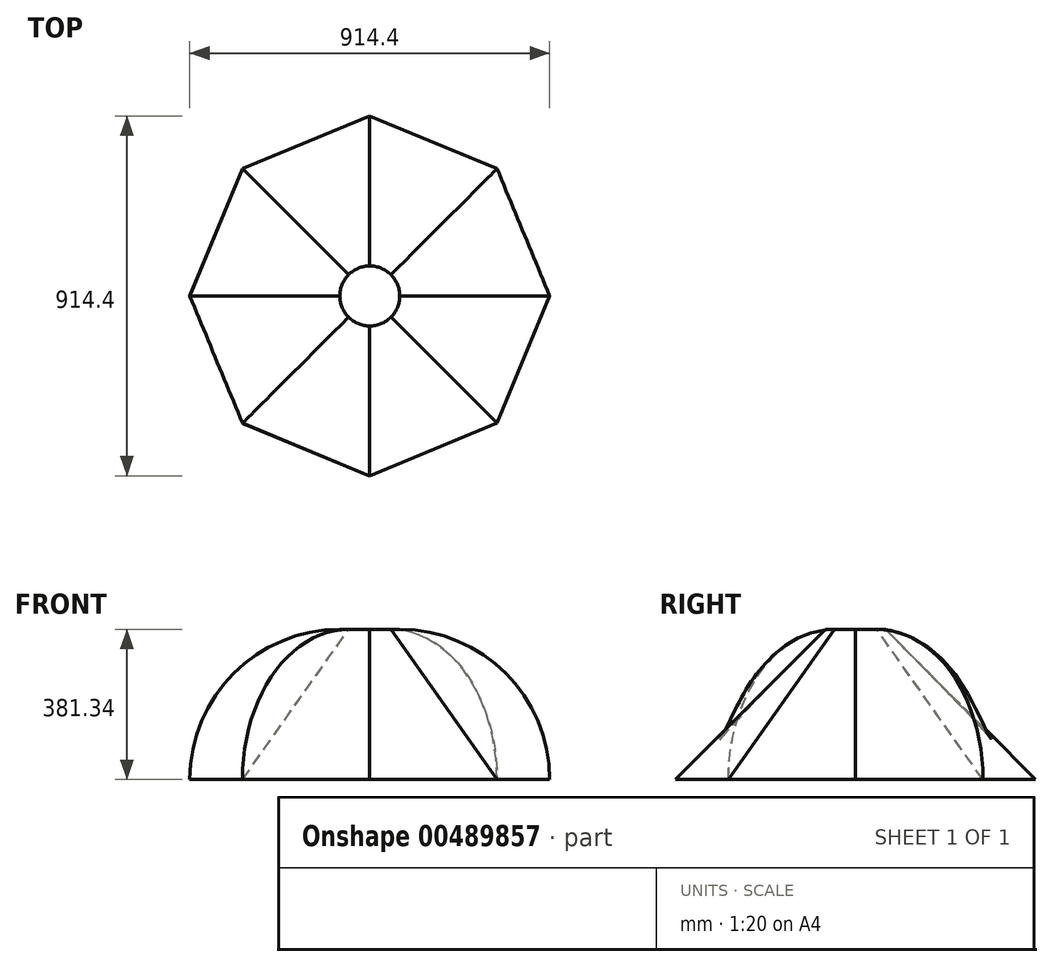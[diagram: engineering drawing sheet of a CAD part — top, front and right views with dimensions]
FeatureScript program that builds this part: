
annotation { "Feature Type Name" : "Feature", "Feature Type Description" : "" }
export const myFeature = defineFeature(function(context is Context, id is Id, definition is map)
    precondition{}
    {
        {
            var Q0;
            Q0=qCreatedBy(makeId("Top.planeOp"),FACE);
            cPlane(context, id + "F0", {"entities" : qUnion([Q0]), "cplaneType" : CPlaneType.OFFSET, "offset" : 381 * mm, "width" : 152.4 * mm, "height" : 152.4 * mm});
        }
        {
            var Q0;
            Q0=qCreatedBy(id+"F0.planeOp",FACE);
            var sketch = newSketch(context, id + "F1", { "sketchPlane" : qUnion([Q0])});
            skCircle(sketch, "E0", {"center": v(0, 0) * mm, "radius": 76.2 * mm});
            skLineSegment(sketch, "E1", {"start": v(0, 76.2) * mm, "end": v(0, -76.2) * mm, "construction": true});
            skLineSegment(sketch, "E2.1.0", {"start": v(53.88, 53.88) * mm, "end": v(-53.88, -53.88) * mm, "construction": true});
            skLineSegment(sketch, "E2.2.0", {"start": v(76.2, 0) * mm, "end": v(-76.2, 0) * mm, "construction": true});
            skLineSegment(sketch, "E2.3.0", {"start": v(53.88, -53.88) * mm, "end": v(-53.88, 53.88) * mm, "construction": true});
            skLineSegment(sketch, "E2.anchor1", {"start": v(0, 0) * mm, "end": v(0, -76.2) * mm, "construction": true});
            skLineSegment(sketch, "E2.anchor2", {"start": v(0, 0) * mm, "end": v(-53.88, 53.88) * mm, "construction": true});
            skSolve(sketch);
        }
        {
            var Q0;
            Q0=qCreatedBy(makeId("Front.planeOp"),FACE);
            var sketch = newSketch(context, id + "F2", { "sketchPlane" : qUnion([Q0])});
            skLineSegment(sketch, "E3", {"start": v(0, 0) * mm, "end": v(0, 381) * mm, "construction": true});
            skSolve(sketch);
        }
        {
            var Q0;
            Q0=qCreatedBy(makeId("Top.planeOp"),FACE);
            var sketch = newSketch(context, id + "F3", { "sketchPlane" : qUnion([Q0])});
            skCircle(sketch, "E4.cCircle", {"center": v(0, 0) * mm, "radius": 422.4 * mm, "construction": true});
            skLineSegment(sketch, "E4.0", {"start": v(323.29, 323.29) * mm, "end": v(457.2, 0) * mm});
            skLineSegment(sketch, "E4.1", {"start": v(457.2, 0) * mm, "end": v(323.29, -323.29) * mm});
            skLineSegment(sketch, "E4.2", {"start": v(323.29, -323.29) * mm, "end": v(0, -457.2) * mm});
            skLineSegment(sketch, "E4.3", {"start": v(0, -457.2) * mm, "end": v(-323.29, -323.29) * mm});
            skLineSegment(sketch, "E4.4", {"start": v(-323.29, -323.29) * mm, "end": v(-457.2, 0) * mm});
            skLineSegment(sketch, "E4.5", {"start": v(-457.2, 0) * mm, "end": v(-323.29, 323.29) * mm});
            skLineSegment(sketch, "E4.6", {"start": v(-323.29, 323.29) * mm, "end": v(0, 457.2) * mm});
            skLineSegment(sketch, "E4.7", {"start": v(0, 457.2) * mm, "end": v(323.29, 323.29) * mm});
            skPoint(sketch, "E4.0.midPoint", {"position": v(390.24, 161.64) * mm});
            skLineSegment(sketch, "E5", {"start": v(0, 457.2) * mm, "end": v(0, -457.2) * mm, "construction": true});
            skSolve(sketch);
        }
        {
            var Q0;
            Q0=qCreatedBy(makeId("Front.planeOp"),FACE);
            var sketch = newSketch(context, id + "F4", { "sketchPlane" : qUnion([Q0])});
            skArc(sketch, "E6", {"start": v(457.2, 0) * mm, "mid": v(345.6, 269.4) * mm, "end": v(76.2, 381) * mm});
            skArc(sketch, "E7.MirrorCS", {"start": v(-457.2, 0) * mm, "mid": v(-345.6, 269.4) * mm, "end": v(-76.2, 381) * mm});
            skSolve(sketch);
        }
        {
            var Q0;
            Q0=qCreatedBy(makeId("Front.planeOp"),FACE);
            var Q1;
            Q1=sQuery(id+"F2.wireOp",EDGE,"E3");
            cPlane(context, id + "F5", {"entities" : qUnion([Q0, Q1]), "cplaneType" : CPlaneType.LINE_ANGLE, "offset" : 25.4 * mm, "angle" : 45 * degree, "width" : 152.4 * mm, "height" : 152.4 * mm});
        }
        {
            var Q0;
            Q0=qCreatedBy(id+"F5.planeOp",FACE);
            var sketch = newSketch(context, id + "F6", { "sketchPlane" : qUnion([Q0])});
            skArc(sketch, "E8", {"start": v(-76.2, 381) * mm, "mid": v(-345.6, 269.4) * mm, "end": v(-457.2, 0) * mm});
            skArc(sketch, "E9.MirrorCS", {"start": v(76.2, 381) * mm, "mid": v(345.6, 269.4) * mm, "end": v(457.2, 0) * mm});
            skSolve(sketch);
        }
        {
            var Q0;
            Q0=qCreatedBy(makeId("Front.planeOp"),FACE);
            var sketch = newSketch(context, id + "F7", { "sketchPlane" : qUnion([Q0])});
            skLineSegment(sketch, "E10", {"start": v(0, 381) * mm, "end": v(0, -533.4) * mm});
            skArc(sketch, "E11", {"start": v(-101.6, -533.4) * mm, "mid": v(-50.8, -584.2) * mm, "end": v(0, -533.4) * mm});
            skSolve(sketch);
        }
        {
            var Q0;
            Q0=qCreatedBy(id+"F0.planeOp",FACE);
            var sketch = newSketch(context, id + "F8", { "sketchPlane" : qUnion([Q0])});
            skCircle(sketch, "E12", {"center": v(0, 0) * mm, "radius": 19.05 * mm});
            skSolve(sketch);
        }
        {
            var Q0;
            Q0=makeQuery(id+"F3.imprint","IMPRINT",FACE,{"disambiguationData":[TD([[makeQuery(id+"F3.imprint","IMPRINT",EDGE,{"derivedFrom":sQuery(id+"F3.wireOp",EDGE,"E4.0")}),-1.0]])]});
            var Q1;
            Q1=makeQuery(id+"F1.imprint","IMPRINT",FACE,{"disambiguationData":[TD([[makeQuery(id+"F1.imprint","IMPRINT",EDGE,{"derivedFrom":sQuery(id+"F1.wireOp",EDGE,"E0")}),1.0]])]});
            var Q2;
            Q2=sQuery(id+"F4.wireOp",EDGE,"E6");
            var Q3;
            Q3=sQuery(id+"FwEUsNg9eqqxYRy_0.1.F6.wireOp",EDGE,"E9.MirrorCS");
            var Q4;
            Q4=sQuery(id+"FwEUsNg9eqqxYRy_0.1.F4.wireOp",EDGE,"E7.MirrorCS");
            var Q5;
            Q5=sQuery(id+"F6.wireOp",EDGE,"E9.MirrorCS");
            var Q6;
            Q6=sQuery(id+"F6.wireOp",EDGE,"E8");
            var Q7;
            Q7=sQuery(id+"FwEUsNg9eqqxYRy_0.1.F4.wireOp",EDGE,"E6");
            var Q8;
            Q8=sQuery(id+"FwEUsNg9eqqxYRy_0.1.F6.wireOp",EDGE,"E8");
            var Q9;
            Q9=sQuery(id+"F4.wireOp",EDGE,"E7.MirrorCS");
            loft(context, id + "F9", {"addGuides" : true, "sheetProfilesArray" : [{ "sheetProfileEntities" : qUnion([Q0]) }, { "sheetProfileEntities" : qUnion([Q1]) }], "guidesArray" : [{ "guideEntities" : qUnion([Q2]), "guideDerivativeType" : LoftGuideDerivativeType.DEFAULT, "guideDerivativeMagnitude" : 1 }, { "guideEntities" : qUnion([Q3]), "guideDerivativeType" : LoftGuideDerivativeType.DEFAULT, "guideDerivativeMagnitude" : 1 }, { "guideEntities" : qUnion([Q4]), "guideDerivativeType" : LoftGuideDerivativeType.DEFAULT, "guideDerivativeMagnitude" : 1 }, { "guideEntities" : qUnion([Q5]), "guideDerivativeType" : LoftGuideDerivativeType.DEFAULT, "guideDerivativeMagnitude" : 1 }, { "guideEntities" : qUnion([Q6]), "guideDerivativeType" : LoftGuideDerivativeType.DEFAULT, "guideDerivativeMagnitude" : 1 }, { "guideEntities" : qUnion([Q7]), "guideDerivativeType" : LoftGuideDerivativeType.DEFAULT, "guideDerivativeMagnitude" : 1 }, { "guideEntities" : qUnion([Q8]), "guideDerivativeType" : LoftGuideDerivativeType.DEFAULT, "guideDerivativeMagnitude" : 1 }, { "guideEntities" : qUnion([Q9]), "guideDerivativeType" : LoftGuideDerivativeType.DEFAULT, "guideDerivativeMagnitude" : 1 }]});
        }
        {
            var Q0;
            Q0=makeQuery(id+"F9.opLoft","CAP_FACE",FACE,{"disambiguationData":[OSD([makeQuery(id+"F3.imprint","IMPRINT",FACE,{"disambiguationData":[TD([[makeQuery(id+"F3.imprint","IMPRINT",EDGE,{"derivedFrom":sQuery(id+"F3.wireOp",EDGE,"E4.0")}),-1.0]])]})])],"isStart":true});
            shell(context, id + "F10", {"entities" : qUnion([Q0]), "thickness" : 0.5 * mm});
        }
        {
            var Q0;
            Q0=makeQuery(id+"F1.imprint","IMPRINT",FACE,{"disambiguationData":[TD([[makeQuery(id+"F1.imprint","IMPRINT",EDGE,{"derivedFrom":sQuery(id+"F1.wireOp",EDGE,"E0")}),1.0]])]});
            var Q1;
            Q1=makeQuery(id+"F3.imprint","IMPRINT",FACE,{"disambiguationData":[TD([[makeQuery(id+"F3.imprint","IMPRINT",EDGE,{"derivedFrom":sQuery(id+"F3.wireOp",EDGE,"E4.0")}),-1.0]])]});
            var Q2;
            Q2=sQuery(id+"F4.wireOp",EDGE,"E6");
            var Q3;
            Q3=sQuery(id+"F4.wireOp",EDGE,"E7.MirrorCS");
            var Q4;
            Q4=sQuery(id+"FwEUsNg9eqqxYRy_0.1.F6.wireOp",EDGE,"E8");
            var Q5;
            Q5=sQuery(id+"FwEUsNg9eqqxYRy_0.1.F4.wireOp",EDGE,"E6");
            var Q6;
            Q6=sQuery(id+"F6.wireOp",EDGE,"E8");
            var Q7;
            Q7=sQuery(id+"FwEUsNg9eqqxYRy_0.1.F6.wireOp",EDGE,"E9.MirrorCS");
            var Q8;
            Q8=sQuery(id+"FwEUsNg9eqqxYRy_0.1.F4.wireOp",EDGE,"E7.MirrorCS");
            var Q9;
            Q9=sQuery(id+"F6.wireOp",EDGE,"E9.MirrorCS");
            loft(context, id + "F11", {"addGuides" : true, "sheetProfilesArray" : [{ "sheetProfileEntities" : qUnion([Q0]) }, { "sheetProfileEntities" : qUnion([Q1]) }], "guidesArray" : [{ "guideEntities" : qUnion([Q2]), "guideDerivativeType" : LoftGuideDerivativeType.DEFAULT, "guideDerivativeMagnitude" : 1 }, { "guideEntities" : qUnion([Q3]), "guideDerivativeType" : LoftGuideDerivativeType.DEFAULT, "guideDerivativeMagnitude" : 1 }, { "guideEntities" : qUnion([Q4]), "guideDerivativeType" : LoftGuideDerivativeType.DEFAULT, "guideDerivativeMagnitude" : 1 }, { "guideEntities" : qUnion([Q5]), "guideDerivativeType" : LoftGuideDerivativeType.DEFAULT, "guideDerivativeMagnitude" : 1 }, { "guideEntities" : qUnion([Q6]), "guideDerivativeType" : LoftGuideDerivativeType.DEFAULT, "guideDerivativeMagnitude" : 1 }, { "guideEntities" : qUnion([Q7]), "guideDerivativeType" : LoftGuideDerivativeType.DEFAULT, "guideDerivativeMagnitude" : 1 }, { "guideEntities" : qUnion([Q8]), "guideDerivativeType" : LoftGuideDerivativeType.DEFAULT, "guideDerivativeMagnitude" : 1 }, { "guideEntities" : qUnion([Q9]), "guideDerivativeType" : LoftGuideDerivativeType.DEFAULT, "guideDerivativeMagnitude" : 1 }]});
        }
    });
